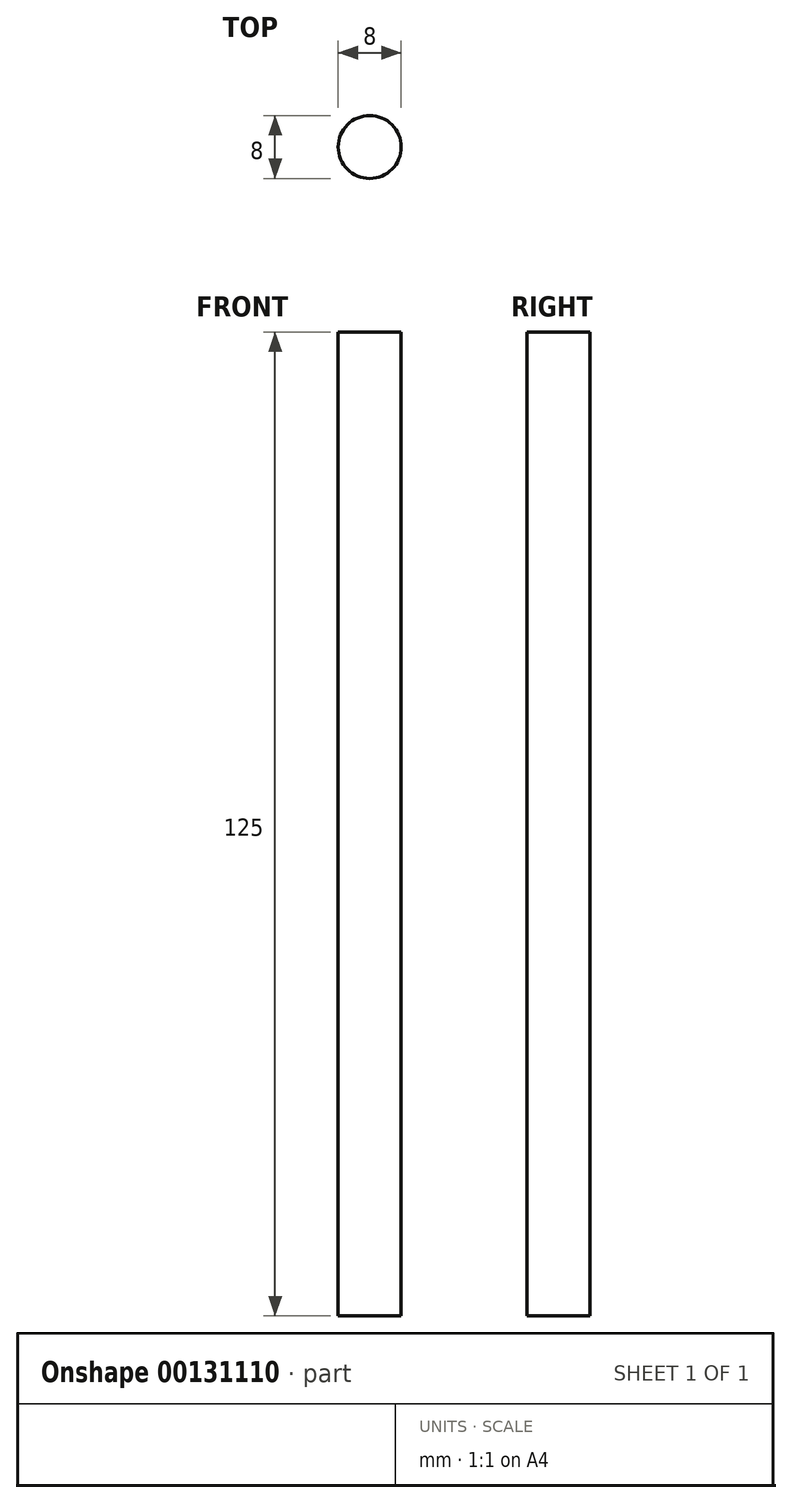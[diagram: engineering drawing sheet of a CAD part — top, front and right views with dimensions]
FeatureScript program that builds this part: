
annotation { "Feature Type Name" : "Feature", "Feature Type Description" : "" }
export const myFeature = defineFeature(function(context is Context, id is Id, definition is map)
    precondition{}
    {
        {
            var Q0;
            Q0=qCreatedBy(makeId("Top.planeOp"),FACE);
            var sketch = newSketch(context, id + "F0", { "sketchPlane" : qUnion([Q0])});
            skCircle(sketch, "E0", {"center": v(0, 0) * mm, "radius": 4 * mm});
            skSolve(sketch);
        }
        {
            var Q0;
            Q0=makeQuery(id+"F0.imprint","IMPRINT",FACE,{"disambiguationData":[TD([[makeQuery(id+"F0.imprint","IMPRINT",EDGE,{"derivedFrom":sQuery(id+"F0.wireOp",EDGE,"E0")}),1.0]])]});
            extrude(context, id + "F1", {"entities" : qUnion([Q0]), "depth" : 125 * mm});
        }
    });
